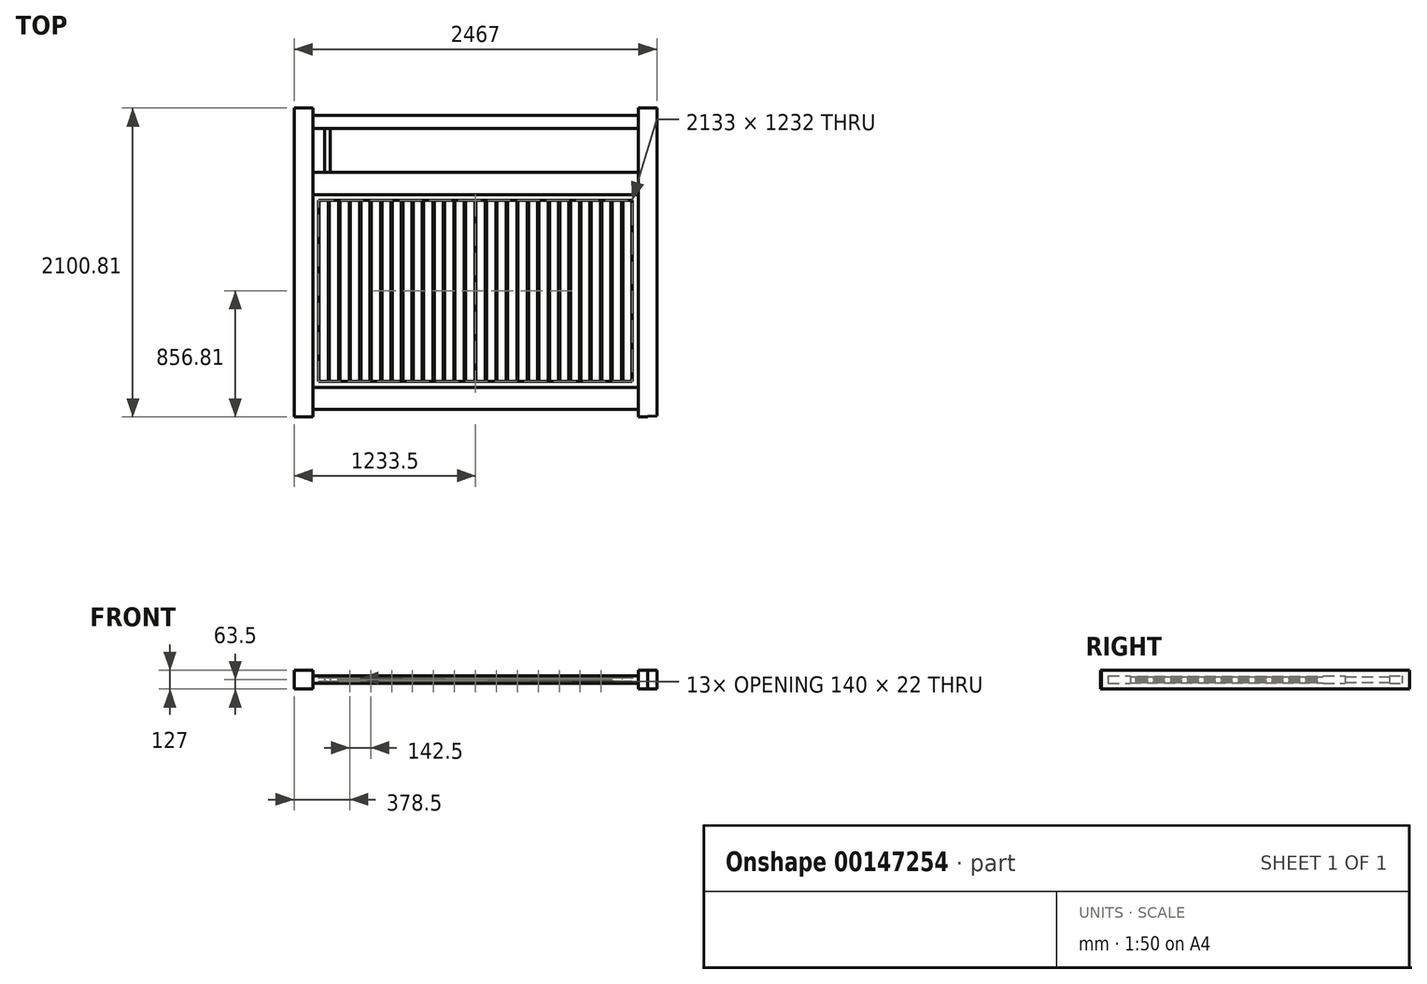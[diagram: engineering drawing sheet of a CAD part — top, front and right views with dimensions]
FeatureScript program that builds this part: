
annotation { "Feature Type Name" : "Feature", "Feature Type Description" : "" }
export const myFeature = defineFeature(function(context is Context, id is Id, definition is map)
    precondition{}
    {
        {
            var Q0;
            Q0=qCreatedBy(makeId("Top.planeOp"),FACE);
            var sketch = newSketch(context, id + "F0", { "sketchPlane" : qUnion([Q0])});
            skLineSegment(sketch, "E0.bottom", {"start": v(1170, -1050) * mm, "end": v(1106.5, -1050) * mm});
            skLineSegment(sketch, "E0.top", {"start": v(1170, 1050) * mm, "end": v(1106.5, 1050) * mm});
            skLineSegment(sketch, "E0.left", {"start": v(1170, -1050) * mm, "end": v(1170, -1047.62) * mm});
            skPoint(sketch, "E0.middle", {"position": v(0, 0) * mm});
            skLineSegment(sketch, "E1", {"start": v(-1170, 1050) * mm, "end": v(-1233.5, 1050) * mm});
            skLineSegment(sketch, "E2", {"start": v(-1233.5, 1050) * mm, "end": v(-1233.5, -1050.8) * mm});
            skLineSegment(sketch, "E3", {"start": v(-1233.5, -1050.8) * mm, "end": v(-1106.5, -1050) * mm});
            skLineSegment(sketch, "E4", {"start": v(-1106.5, -1050) * mm, "end": v(-1106.5, 1050) * mm});
            skLineSegment(sketch, "E5", {"start": v(-1106.5, 1050) * mm, "end": v(-1233.5, 1050) * mm});
            skLineSegment(sketch, "E6", {"start": v(1106.5, -1050) * mm, "end": v(1106.5, 1050) * mm});
            skLineSegment(sketch, "E7", {"start": v(1106.5, 1050) * mm, "end": v(1233.5, 1050) * mm});
            skLineSegment(sketch, "E8", {"start": v(1233.5, 1050) * mm, "end": v(1233.5, -1045.25) * mm});
            skLineSegment(sketch, "E9", {"start": v(1233.5, -1045.25) * mm, "end": v(1106.5, -1050) * mm});
            skLineSegment(sketch, "E10", {"start": v(-1106.5, 1000) * mm, "end": v(1106.5, 1000) * mm});
            skLineSegment(sketch, "E11", {"start": v(1106.5, 1000) * mm, "end": v(1106.5, 912) * mm});
            skLineSegment(sketch, "E12", {"start": v(1106.5, 912) * mm, "end": v(-1106.5, 912) * mm});
            skLineSegment(sketch, "E13", {"start": v(-1106.5, 912) * mm, "end": v(-1106.5, 1000) * mm});
            skLineSegment(sketch, "E14", {"start": v(-1106.5, 612) * mm, "end": v(1106.5, 612) * mm});
            skLineSegment(sketch, "E15", {"start": v(1106.5, 612) * mm, "end": v(1106.5, 462) * mm});
            skLineSegment(sketch, "E16", {"start": v(1106.5, 462) * mm, "end": v(-1106.5, 462) * mm});
            skLineSegment(sketch, "E17", {"start": v(-1106.5, 462) * mm, "end": v(-1106.5, 612) * mm});
            skLineSegment(sketch, "E18", {"start": v(-1106.5, -1000) * mm, "end": v(1106.5, -1000) * mm});
            skLineSegment(sketch, "E19", {"start": v(1106.5, -1000) * mm, "end": v(1106.5, -850) * mm});
            skLineSegment(sketch, "E20", {"start": v(1106.5, -850) * mm, "end": v(-1106.5, -850) * mm});
            skLineSegment(sketch, "E21", {"start": v(-1106.5, -850) * mm, "end": v(-1106.5, -1000) * mm});
            skLineSegment(sketch, "E22", {"start": v(-1106.5, -810) * mm, "end": v(1106.5, -810) * mm});
            skLineSegment(sketch, "E23", {"start": v(-1106.5, 422) * mm, "end": v(1106.5, 422) * mm});
            skLineSegment(sketch, "E24", {"start": v(-1066.5, 422) * mm, "end": v(-1066.5, -810) * mm});
            skLineSegment(sketch, "E25", {"start": v(1066.5, 422) * mm, "end": v(1066.5, -810) * mm});
            skLineSegment(sketch, "E26.trimOffspring", {"start": v(-1106.5, 1050) * mm, "end": v(-1170, 1050) * mm});
            skLineSegment(sketch, "E27.trimOffspring", {"start": v(-1106.5, -1050) * mm, "end": v(-1170, -1050) * mm});
            skLineSegment(sketch, "E28", {"start": v(-1106.5, 1000) * mm, "end": v(-1106.5, 912) * mm});
            skLineSegment(sketch, "E29", {"start": v(1106.5, 912) * mm, "end": v(1106.5, 1000) * mm});
            skLineSegment(sketch, "E30", {"start": v(-1026.03, 912) * mm, "end": v(-1026.03, 612) * mm});
            skLineSegment(sketch, "E31", {"start": v(-1026.03, 612) * mm, "end": v(-988.03, 612) * mm});
            skLineSegment(sketch, "E32", {"start": v(-988.03, 612) * mm, "end": v(-988.03, 912) * mm});
            skLineSegment(sketch, "E33", {"start": v(-988.03, 912) * mm, "end": v(-1026.03, 912) * mm});
            skLineSegment(sketch, "E34.1.0.0", {"start": v(-869.56, 912) * mm, "end": v(-907.56, 912) * mm});
            skLineSegment(sketch, "E34.1.0.1", {"start": v(-907.56, 912) * mm, "end": v(-907.56, 612) * mm});
            skLineSegment(sketch, "E34.1.0.2", {"start": v(-869.56, 612) * mm, "end": v(-869.56, 912) * mm});
            skLineSegment(sketch, "E34.1.0.3", {"start": v(-907.56, 612) * mm, "end": v(-869.56, 612) * mm});
            skLineSegment(sketch, "E34.2.0.0", {"start": v(-751.1, 912) * mm, "end": v(-789.1, 912) * mm});
            skLineSegment(sketch, "E34.2.0.1", {"start": v(-789.1, 912) * mm, "end": v(-789.1, 612) * mm});
            skLineSegment(sketch, "E34.2.0.2", {"start": v(-751.1, 612) * mm, "end": v(-751.1, 912) * mm});
            skLineSegment(sketch, "E34.2.0.3", {"start": v(-789.1, 612) * mm, "end": v(-751.1, 612) * mm});
            skLineSegment(sketch, "E34.3.0.0", {"start": v(-632.62, 912) * mm, "end": v(-670.62, 912) * mm});
            skLineSegment(sketch, "E34.3.0.1", {"start": v(-670.62, 912) * mm, "end": v(-670.62, 612) * mm});
            skLineSegment(sketch, "E34.3.0.2", {"start": v(-632.62, 612) * mm, "end": v(-632.62, 912) * mm});
            skLineSegment(sketch, "E34.3.0.3", {"start": v(-670.62, 612) * mm, "end": v(-632.62, 612) * mm});
            skLineSegment(sketch, "E34.4.0.0", {"start": v(-514.15, 912) * mm, "end": v(-552.15, 912) * mm});
            skLineSegment(sketch, "E34.4.0.1", {"start": v(-552.15, 912) * mm, "end": v(-552.15, 612) * mm});
            skLineSegment(sketch, "E34.4.0.2", {"start": v(-514.15, 612) * mm, "end": v(-514.15, 912) * mm});
            skLineSegment(sketch, "E34.4.0.3", {"start": v(-552.15, 612) * mm, "end": v(-514.15, 612) * mm});
            skLineSegment(sketch, "E34.5.0.0", {"start": v(-395.68, 912) * mm, "end": v(-433.68, 912) * mm});
            skLineSegment(sketch, "E34.5.0.1", {"start": v(-433.68, 912) * mm, "end": v(-433.68, 612) * mm});
            skLineSegment(sketch, "E34.5.0.2", {"start": v(-395.68, 612) * mm, "end": v(-395.68, 912) * mm});
            skLineSegment(sketch, "E34.5.0.3", {"start": v(-433.68, 612) * mm, "end": v(-395.68, 612) * mm});
            skLineSegment(sketch, "E34.6.0.0", {"start": v(-277.21, 912) * mm, "end": v(-315.21, 912) * mm});
            skLineSegment(sketch, "E34.6.0.1", {"start": v(-315.21, 912) * mm, "end": v(-315.21, 612) * mm});
            skLineSegment(sketch, "E34.6.0.2", {"start": v(-277.21, 612) * mm, "end": v(-277.21, 912) * mm});
            skLineSegment(sketch, "E34.6.0.3", {"start": v(-315.21, 612) * mm, "end": v(-277.21, 612) * mm});
            skLineSegment(sketch, "E34.7.0.0", {"start": v(-158.74, 912) * mm, "end": v(-196.74, 912) * mm});
            skLineSegment(sketch, "E34.7.0.1", {"start": v(-196.74, 912) * mm, "end": v(-196.74, 612) * mm});
            skLineSegment(sketch, "E34.7.0.2", {"start": v(-158.74, 612) * mm, "end": v(-158.74, 912) * mm});
            skLineSegment(sketch, "E34.7.0.3", {"start": v(-196.74, 612) * mm, "end": v(-158.74, 612) * mm});
            skLineSegment(sketch, "E34.8.0.0", {"start": v(-40.27, 912) * mm, "end": v(-78.27, 912) * mm});
            skLineSegment(sketch, "E34.8.0.1", {"start": v(-78.27, 912) * mm, "end": v(-78.27, 612) * mm});
            skLineSegment(sketch, "E34.8.0.2", {"start": v(-40.27, 612) * mm, "end": v(-40.27, 912) * mm});
            skLineSegment(sketch, "E34.8.0.3", {"start": v(-78.27, 612) * mm, "end": v(-40.27, 612) * mm});
            skLineSegment(sketch, "E34.9.0.0", {"start": v(78.2, 912) * mm, "end": v(40.2, 912) * mm});
            skLineSegment(sketch, "E34.9.0.1", {"start": v(40.2, 912) * mm, "end": v(40.2, 612) * mm});
            skLineSegment(sketch, "E34.9.0.2", {"start": v(78.2, 612) * mm, "end": v(78.2, 912) * mm});
            skLineSegment(sketch, "E34.9.0.3", {"start": v(40.2, 612) * mm, "end": v(78.2, 612) * mm});
            skLineSegment(sketch, "E34.10.0.0", {"start": v(196.67, 912) * mm, "end": v(158.67, 912) * mm});
            skLineSegment(sketch, "E34.10.0.1", {"start": v(158.67, 912) * mm, "end": v(158.67, 612) * mm});
            skLineSegment(sketch, "E34.10.0.2", {"start": v(196.67, 612) * mm, "end": v(196.67, 912) * mm});
            skLineSegment(sketch, "E34.10.0.3", {"start": v(158.67, 612) * mm, "end": v(196.67, 612) * mm});
            skLineSegment(sketch, "E34.11.0.0", {"start": v(315.14, 912) * mm, "end": v(277.14, 912) * mm});
            skLineSegment(sketch, "E34.11.0.1", {"start": v(277.14, 912) * mm, "end": v(277.14, 612) * mm});
            skLineSegment(sketch, "E34.11.0.2", {"start": v(315.14, 612) * mm, "end": v(315.14, 912) * mm});
            skLineSegment(sketch, "E34.11.0.3", {"start": v(277.14, 612) * mm, "end": v(315.14, 612) * mm});
            skLineSegment(sketch, "E34.12.0.0", {"start": v(433.6, 912) * mm, "end": v(395.6, 912) * mm});
            skLineSegment(sketch, "E34.12.0.1", {"start": v(395.6, 912) * mm, "end": v(395.6, 612) * mm});
            skLineSegment(sketch, "E34.12.0.2", {"start": v(433.6, 612) * mm, "end": v(433.6, 912) * mm});
            skLineSegment(sketch, "E34.12.0.3", {"start": v(395.6, 612) * mm, "end": v(433.6, 612) * mm});
            skLineSegment(sketch, "E34.13.0.0", {"start": v(552.08, 912) * mm, "end": v(514.08, 912) * mm});
            skLineSegment(sketch, "E34.13.0.1", {"start": v(514.08, 912) * mm, "end": v(514.08, 612) * mm});
            skLineSegment(sketch, "E34.13.0.2", {"start": v(552.08, 612) * mm, "end": v(552.08, 912) * mm});
            skLineSegment(sketch, "E34.13.0.3", {"start": v(514.08, 612) * mm, "end": v(552.08, 612) * mm});
            skLineSegment(sketch, "E34.14.0.0", {"start": v(670.55, 912) * mm, "end": v(632.55, 912) * mm});
            skLineSegment(sketch, "E34.14.0.1", {"start": v(632.55, 912) * mm, "end": v(632.55, 612) * mm});
            skLineSegment(sketch, "E34.14.0.2", {"start": v(670.55, 612) * mm, "end": v(670.55, 912) * mm});
            skLineSegment(sketch, "E34.14.0.3", {"start": v(632.55, 612) * mm, "end": v(670.55, 612) * mm});
            skLineSegment(sketch, "E34.15.0.0", {"start": v(789.02, 912) * mm, "end": v(751.02, 912) * mm});
            skLineSegment(sketch, "E34.15.0.1", {"start": v(751.02, 912) * mm, "end": v(751.02, 612) * mm});
            skLineSegment(sketch, "E34.15.0.2", {"start": v(789.02, 612) * mm, "end": v(789.02, 912) * mm});
            skLineSegment(sketch, "E34.15.0.3", {"start": v(751.02, 612) * mm, "end": v(789.02, 612) * mm});
            skLineSegment(sketch, "E34.16.0.0", {"start": v(907.49, 912) * mm, "end": v(869.49, 912) * mm});
            skLineSegment(sketch, "E34.16.0.1", {"start": v(869.49, 912) * mm, "end": v(869.49, 612) * mm});
            skLineSegment(sketch, "E34.16.0.2", {"start": v(907.49, 612) * mm, "end": v(907.49, 912) * mm});
            skLineSegment(sketch, "E34.16.0.3", {"start": v(869.49, 612) * mm, "end": v(907.49, 612) * mm});
            skLineSegment(sketch, "E34.17.0.0", {"start": v(1025.96, 912) * mm, "end": v(987.96, 912) * mm});
            skLineSegment(sketch, "E34.17.0.1", {"start": v(987.96, 912) * mm, "end": v(987.96, 612) * mm});
            skLineSegment(sketch, "E34.17.0.2", {"start": v(1025.96, 612) * mm, "end": v(1025.96, 912) * mm});
            skLineSegment(sketch, "E34.17.0.3", {"start": v(987.96, 612) * mm, "end": v(1025.96, 612) * mm});
            skLineSegment(sketch, "E34.direction1", {"start": v(-1026.03, 912) * mm, "end": v(-907.56, 912) * mm, "construction": true});
            skSolve(sketch);
        }
        {
            var Q0;
            {var subQ0=sQuery(id+"F0.wireOp",EDGE,"E0.left");Q0=makeQuery(id+"F0.imprint","IMPRINT",FACE,{"disambiguationData":[TD([[makeQuery(id+"F0.imprint","IMPRINT",EDGE,{"derivedFrom":subQ0}),1.0]])]});}
            var Q1;
            Q1=makeQuery(id+"F0.imprint","IMPRINT",FACE,{"disambiguationData":[TD([[makeQuery(id+"F0.imprint","IMPRINT",EDGE,{"derivedFrom":sQuery(id+"F0.wireOp",EDGE,"E2")}),1.0]])]});
            var Q2;
            {var subQ6=sQuery(id+"F0.wireOp",EDGE,"E8");Q2=makeQuery(id+"F0.imprint","IMPRINT",FACE,{"disambiguationData":[TD([[makeQuery(id+"F0.imprint","IMPRINT",EDGE,{"derivedFrom":subQ6}),-1.0]])]});}
            extrude(context, id + "F1", {"entities" : qUnion([Q0, Q1, Q2]), "depth" : 63.5 * mm, "hasSecondDirection" : true, "secondDirectionOppositeDirection" : true, "secondDirectionDepth" : 63.5 * mm});
        }
        {
            var Q0;
            Q0=makeQuery(id+"F0.imprint","IMPRINT",FACE,{"disambiguationData":[TD([[makeQuery(id+"F0.imprint","IMPRINT",EDGE,{"derivedFrom":sQuery(id+"F0.wireOp",EDGE,"E10")}),-1.0]])]});
            var Q1;
            Q1=makeQuery(id+"F0.imprint","IMPRINT",FACE,{"disambiguationData":[TD([[makeQuery(id+"F0.imprint","IMPRINT",EDGE,{"derivedFrom":sQuery(id+"F0.wireOp",EDGE,"E14")}),-1.0]])]});
            var Q2;
            Q2=makeQuery(id+"F0.imprint","IMPRINT",FACE,{"disambiguationData":[TD([[makeQuery(id+"F0.imprint","IMPRINT",EDGE,{"derivedFrom":sQuery(id+"F0.wireOp",EDGE,"E18")}),1.0]])]});
            extrude(context, id + "F2", {"entities" : qUnion([Q0, Q1, Q2]), "depth" : 25 * mm, "hasSecondDirection" : true, "secondDirectionOppositeDirection" : true, "secondDirectionDepth" : 25 * mm});
        }
        {
            var Q0;
            {var subQ0=sQuery(id+"F0.wireOp",EDGE,"E16");Q0=makeQuery(id+"F0.imprint","IMPRINT",FACE,{"disambiguationData":[TD([[makeQuery(id+"F0.imprint","IMPRINT",EDGE,{"derivedFrom":subQ0}),1.0]])]});}
            var Q1;
            {var subQ5=sQuery(id+"F0.wireOp",EDGE,"E25");Q1=makeQuery(id+"F0.imprint","IMPRINT",FACE,{"disambiguationData":[TD([[makeQuery(id+"F0.imprint","IMPRINT",EDGE,{"derivedFrom":subQ5}),1.0]])]});}
            var Q2;
            {var subQ4=sQuery(id+"F0.wireOp",EDGE,"E20");Q2=makeQuery(id+"F0.imprint","IMPRINT",FACE,{"disambiguationData":[TD([[makeQuery(id+"F0.imprint","IMPRINT",EDGE,{"derivedFrom":subQ4}),-1.0]])]});}
            var Q3;
            {var subQ5=sQuery(id+"F0.wireOp",EDGE,"E24");Q3=makeQuery(id+"F0.imprint","IMPRINT",FACE,{"disambiguationData":[TD([[makeQuery(id+"F0.imprint","IMPRINT",EDGE,{"derivedFrom":subQ5}),-1.0]])]});}
            extrude(context, id + "F3", {"entities" : qUnion([Q0, Q1, Q2, Q3]), "depth" : 20 * mm, "hasSecondDirection" : true, "secondDirectionOppositeDirection" : true, "secondDirectionDepth" : 20 * mm});
        }
        {
            var Q0;
            Q0=makeQuery(id+"F0.imprint","IMPRINT",FACE,{"disambiguationData":[TD([[makeQuery(id+"F0.imprint","IMPRINT",EDGE,{"derivedFrom":sQuery(id+"F0.wireOp",EDGE,"E30")}),1.0]])]});
            var Q1;
            Q1=makeQuery(id+"F0.imprint","IMPRINT",FACE,{"disambiguationData":[TD([[makeQuery(id+"F0.imprint","IMPRINT",EDGE,{"derivedFrom":sQuery(id+"F0.wireOp",EDGE,"E34.1.0.0")}),1.0]])]});
            var Q2;
            Q2=makeQuery(id+"F0.imprint","IMPRINT",FACE,{"disambiguationData":[TD([[makeQuery(id+"F0.imprint","IMPRINT",EDGE,{"derivedFrom":sQuery(id+"F0.wireOp",EDGE,"E34.2.0.0")}),1.0]])]});
            var Q3;
            Q3=makeQuery(id+"F0.imprint","IMPRINT",FACE,{"disambiguationData":[TD([[makeQuery(id+"F0.imprint","IMPRINT",EDGE,{"derivedFrom":sQuery(id+"F0.wireOp",EDGE,"E34.3.0.0")}),1.0]])]});
            var Q4;
            Q4=makeQuery(id+"F0.imprint","IMPRINT",FACE,{"disambiguationData":[TD([[makeQuery(id+"F0.imprint","IMPRINT",EDGE,{"derivedFrom":sQuery(id+"F0.wireOp",EDGE,"E34.4.0.0")}),1.0]])]});
            var Q5;
            Q5=makeQuery(id+"F0.imprint","IMPRINT",FACE,{"disambiguationData":[TD([[makeQuery(id+"F0.imprint","IMPRINT",EDGE,{"derivedFrom":sQuery(id+"F0.wireOp",EDGE,"E34.5.0.0")}),1.0]])]});
            var Q6;
            Q6=makeQuery(id+"F0.imprint","IMPRINT",FACE,{"disambiguationData":[TD([[makeQuery(id+"F0.imprint","IMPRINT",EDGE,{"derivedFrom":sQuery(id+"F0.wireOp",EDGE,"E34.6.0.0")}),1.0]])]});
            var Q7;
            Q7=makeQuery(id+"F0.imprint","IMPRINT",FACE,{"disambiguationData":[TD([[makeQuery(id+"F0.imprint","IMPRINT",EDGE,{"derivedFrom":sQuery(id+"F0.wireOp",EDGE,"E34.7.0.0")}),1.0]])]});
            var Q8;
            Q8=makeQuery(id+"F0.imprint","IMPRINT",FACE,{"disambiguationData":[TD([[makeQuery(id+"F0.imprint","IMPRINT",EDGE,{"derivedFrom":sQuery(id+"F0.wireOp",EDGE,"E34.8.0.0")}),1.0]])]});
            var Q9;
            Q9=makeQuery(id+"F0.imprint","IMPRINT",FACE,{"disambiguationData":[TD([[makeQuery(id+"F0.imprint","IMPRINT",EDGE,{"derivedFrom":sQuery(id+"F0.wireOp",EDGE,"E34.9.0.0")}),1.0]])]});
            var Q10;
            Q10=makeQuery(id+"F0.imprint","IMPRINT",FACE,{"disambiguationData":[TD([[makeQuery(id+"F0.imprint","IMPRINT",EDGE,{"derivedFrom":sQuery(id+"F0.wireOp",EDGE,"E34.10.0.0")}),1.0]])]});
            var Q11;
            Q11=makeQuery(id+"F0.imprint","IMPRINT",FACE,{"disambiguationData":[TD([[makeQuery(id+"F0.imprint","IMPRINT",EDGE,{"derivedFrom":sQuery(id+"F0.wireOp",EDGE,"E34.11.0.0")}),1.0]])]});
            var Q12;
            Q12=makeQuery(id+"F0.imprint","IMPRINT",FACE,{"disambiguationData":[TD([[makeQuery(id+"F0.imprint","IMPRINT",EDGE,{"derivedFrom":sQuery(id+"F0.wireOp",EDGE,"E34.12.0.0")}),1.0]])]});
            var Q13;
            Q13=makeQuery(id+"F0.imprint","IMPRINT",FACE,{"disambiguationData":[TD([[makeQuery(id+"F0.imprint","IMPRINT",EDGE,{"derivedFrom":sQuery(id+"F0.wireOp",EDGE,"E34.13.0.0")}),1.0]])]});
            var Q14;
            Q14=makeQuery(id+"F0.imprint","IMPRINT",FACE,{"disambiguationData":[TD([[makeQuery(id+"F0.imprint","IMPRINT",EDGE,{"derivedFrom":sQuery(id+"F0.wireOp",EDGE,"E34.14.0.0")}),1.0]])]});
            var Q15;
            Q15=makeQuery(id+"F0.imprint","IMPRINT",FACE,{"disambiguationData":[TD([[makeQuery(id+"F0.imprint","IMPRINT",EDGE,{"derivedFrom":sQuery(id+"F0.wireOp",EDGE,"E34.15.0.0")}),1.0]])]});
            var Q16;
            Q16=makeQuery(id+"F0.imprint","IMPRINT",FACE,{"disambiguationData":[TD([[makeQuery(id+"F0.imprint","IMPRINT",EDGE,{"derivedFrom":sQuery(id+"F0.wireOp",EDGE,"E34.16.0.0")}),1.0]])]});
            var Q17;
            Q17=makeQuery(id+"F0.imprint","IMPRINT",FACE,{"disambiguationData":[TD([[makeQuery(id+"F0.imprint","IMPRINT",EDGE,{"derivedFrom":sQuery(id+"F0.wireOp",EDGE,"E34.17.0.0")}),1.0]])]});
            extrude(context, id + "F4", {"entities" : qUnion([Q0, Q1, Q2, Q3, Q4, Q5, Q6, Q7, Q8, Q9, Q10, Q11, Q12, Q13, Q14, Q15, Q16, Q17]), "depth" : 19 * mm, "hasSecondDirection" : true, "secondDirectionOppositeDirection" : true, "secondDirectionDepth" : 19 * mm});
        }
        {
            var Q0;
            Q0=qCreatedBy(makeId("Front.planeOp"),FACE);
            var sketch = newSketch(context, id + "F5", { "sketchPlane" : qUnion([Q0])});
            skLineSegment(sketch, "E35.bottom", {"start": v(-931.2, -11) * mm, "end": v(-992.5, -11) * mm});
            skLineSegment(sketch, "E35.top", {"start": v(-930.95, 11) * mm, "end": v(-993.4, 11) * mm});
            skLineSegment(sketch, "E35.left", {"start": v(-927.5, -7.64) * mm, "end": v(-927.5, 7.38) * mm});
            skLineSegment(sketch, "E35.right", {"start": v(-1067.5, -8.32) * mm, "end": v(-1067.5, 7.65) * mm});
            skLineSegment(sketch, "E36", {"start": v(-1063.8, 11) * mm, "end": v(-1067.5, 7.65) * mm});
            skLineSegment(sketch, "E37", {"start": v(-1067.5, -8.32) * mm, "end": v(-1063.28, -11) * mm});
            skLineSegment(sketch, "E38", {"start": v(-930.95, 11) * mm, "end": v(-927.5, 7.38) * mm});
            skLineSegment(sketch, "E39", {"start": v(-927.5, -7.64) * mm, "end": v(-931.2, -11) * mm});
            skPoint(sketch, "E40.orphan", {"position": v(-927.5, -11) * mm});
            skPoint(sketch, "E41.orphan", {"position": v(-927.5, 11) * mm});
            skPoint(sketch, "E42.orphan", {"position": v(-1067.5, -11) * mm});
            skPoint(sketch, "E43.orphan", {"position": v(-1067.5, 11) * mm});
            skLineSegment(sketch, "E44", {"start": v(-1000.5, -11) * mm, "end": v(-996.5, -8) * mm});
            skLineSegment(sketch, "E45", {"start": v(-996.5, -8) * mm, "end": v(-992.5, -11) * mm});
            skLineSegment(sketch, "E46", {"start": v(-1001.4, 11) * mm, "end": v(-997.4, 8) * mm});
            skLineSegment(sketch, "E47", {"start": v(-997.4, 8) * mm, "end": v(-993.4, 11) * mm});
            skLineSegment(sketch, "E48.trimOffspring", {"start": v(-1001.4, 11) * mm, "end": v(-1063.8, 11) * mm});
            skPoint(sketch, "E49.orphan", {"position": v(0, 18.02) * mm});
            skLineSegment(sketch, "E50.trimOffspring", {"start": v(-1000.5, -11) * mm, "end": v(-1063.28, -11) * mm});
            skLineSegment(sketch, "E51.1.0.0", {"start": v(-858, -11) * mm, "end": v(-920.78, -11) * mm});
            skLineSegment(sketch, "E51.1.0.1", {"start": v(-925, -8.32) * mm, "end": v(-925, 7.65) * mm});
            skPoint(sketch, "E51.1.0.2", {"position": v(-785, 11) * mm});
            skPoint(sketch, "E51.1.0.3", {"position": v(-925, -11) * mm});
            skLineSegment(sketch, "E51.1.0.4", {"start": v(-785, -7.64) * mm, "end": v(-785, 7.38) * mm});
            skPoint(sketch, "E51.1.0.5", {"position": v(-785, -11) * mm});
            skLineSegment(sketch, "E51.1.0.6", {"start": v(-788.45, 11) * mm, "end": v(-850.9, 11) * mm});
            skLineSegment(sketch, "E51.1.0.7", {"start": v(-788.7, -11) * mm, "end": v(-850, -11) * mm});
            skLineSegment(sketch, "E51.1.0.8", {"start": v(-858.9, 11) * mm, "end": v(-921.3, 11) * mm});
            skPoint(sketch, "E51.1.0.9", {"position": v(-925, 11) * mm});
            skLineSegment(sketch, "E51.1.0.10", {"start": v(-921.3, 11) * mm, "end": v(-925, 7.65) * mm});
            skLineSegment(sketch, "E51.1.0.11", {"start": v(-854, -8) * mm, "end": v(-850, -11) * mm});
            skLineSegment(sketch, "E51.1.0.12", {"start": v(-925, -8.32) * mm, "end": v(-920.78, -11) * mm});
            skLineSegment(sketch, "E51.1.0.13", {"start": v(-788.45, 11) * mm, "end": v(-785, 7.38) * mm});
            skLineSegment(sketch, "E51.1.0.14", {"start": v(-858, -11) * mm, "end": v(-854, -8) * mm});
            skLineSegment(sketch, "E51.1.0.15", {"start": v(-785, -7.64) * mm, "end": v(-788.7, -11) * mm});
            skLineSegment(sketch, "E51.1.0.16", {"start": v(-854.9, 8) * mm, "end": v(-850.9, 11) * mm});
            skLineSegment(sketch, "E51.1.0.17", {"start": v(-858.9, 11) * mm, "end": v(-854.9, 8) * mm});
            skLineSegment(sketch, "E51.2.0.0", {"start": v(-715.5, -11) * mm, "end": v(-778.28, -11) * mm});
            skLineSegment(sketch, "E51.2.0.1", {"start": v(-782.5, -8.32) * mm, "end": v(-782.5, 7.65) * mm});
            skPoint(sketch, "E51.2.0.2", {"position": v(-642.5, 11) * mm});
            skPoint(sketch, "E51.2.0.3", {"position": v(-782.5, -11) * mm});
            skLineSegment(sketch, "E51.2.0.4", {"start": v(-642.5, -7.64) * mm, "end": v(-642.5, 7.38) * mm});
            skPoint(sketch, "E51.2.0.5", {"position": v(-642.5, -11) * mm});
            skLineSegment(sketch, "E51.2.0.6", {"start": v(-645.95, 11) * mm, "end": v(-708.4, 11) * mm});
            skLineSegment(sketch, "E51.2.0.7", {"start": v(-646.2, -11) * mm, "end": v(-707.5, -11) * mm});
            skLineSegment(sketch, "E51.2.0.8", {"start": v(-716.4, 11) * mm, "end": v(-778.8, 11) * mm});
            skPoint(sketch, "E51.2.0.9", {"position": v(-782.5, 11) * mm});
            skLineSegment(sketch, "E51.2.0.10", {"start": v(-778.8, 11) * mm, "end": v(-782.5, 7.65) * mm});
            skLineSegment(sketch, "E51.2.0.11", {"start": v(-711.5, -8) * mm, "end": v(-707.5, -11) * mm});
            skLineSegment(sketch, "E51.2.0.12", {"start": v(-782.5, -8.32) * mm, "end": v(-778.28, -11) * mm});
            skLineSegment(sketch, "E51.2.0.13", {"start": v(-645.95, 11) * mm, "end": v(-642.5, 7.38) * mm});
            skLineSegment(sketch, "E51.2.0.14", {"start": v(-715.5, -11) * mm, "end": v(-711.5, -8) * mm});
            skLineSegment(sketch, "E51.2.0.15", {"start": v(-642.5, -7.64) * mm, "end": v(-646.2, -11) * mm});
            skLineSegment(sketch, "E51.2.0.16", {"start": v(-712.4, 8) * mm, "end": v(-708.4, 11) * mm});
            skLineSegment(sketch, "E51.2.0.17", {"start": v(-716.4, 11) * mm, "end": v(-712.4, 8) * mm});
            skLineSegment(sketch, "E51.3.0.0", {"start": v(-573, -11) * mm, "end": v(-635.78, -11) * mm});
            skLineSegment(sketch, "E51.3.0.1", {"start": v(-640, -8.32) * mm, "end": v(-640, 7.65) * mm});
            skPoint(sketch, "E51.3.0.2", {"position": v(-500, 11) * mm});
            skPoint(sketch, "E51.3.0.3", {"position": v(-640, -11) * mm});
            skLineSegment(sketch, "E51.3.0.4", {"start": v(-500, -7.64) * mm, "end": v(-500, 7.38) * mm});
            skPoint(sketch, "E51.3.0.5", {"position": v(-500, -11) * mm});
            skLineSegment(sketch, "E51.3.0.6", {"start": v(-503.45, 11) * mm, "end": v(-565.9, 11) * mm});
            skLineSegment(sketch, "E51.3.0.7", {"start": v(-503.7, -11) * mm, "end": v(-565, -11) * mm});
            skLineSegment(sketch, "E51.3.0.8", {"start": v(-573.9, 11) * mm, "end": v(-636.3, 11) * mm});
            skPoint(sketch, "E51.3.0.9", {"position": v(-640, 11) * mm});
            skLineSegment(sketch, "E51.3.0.10", {"start": v(-636.3, 11) * mm, "end": v(-640, 7.65) * mm});
            skLineSegment(sketch, "E51.3.0.11", {"start": v(-569, -8) * mm, "end": v(-565, -11) * mm});
            skLineSegment(sketch, "E51.3.0.12", {"start": v(-640, -8.32) * mm, "end": v(-635.78, -11) * mm});
            skLineSegment(sketch, "E51.3.0.13", {"start": v(-503.45, 11) * mm, "end": v(-500, 7.38) * mm});
            skLineSegment(sketch, "E51.3.0.14", {"start": v(-573, -11) * mm, "end": v(-569, -8) * mm});
            skLineSegment(sketch, "E51.3.0.15", {"start": v(-500, -7.64) * mm, "end": v(-503.7, -11) * mm});
            skLineSegment(sketch, "E51.3.0.16", {"start": v(-569.9, 8) * mm, "end": v(-565.9, 11) * mm});
            skLineSegment(sketch, "E51.3.0.17", {"start": v(-573.9, 11) * mm, "end": v(-569.9, 8) * mm});
            skLineSegment(sketch, "E51.4.0.0", {"start": v(-430.5, -11) * mm, "end": v(-493.28, -11) * mm});
            skLineSegment(sketch, "E51.4.0.1", {"start": v(-497.5, -8.32) * mm, "end": v(-497.5, 7.65) * mm});
            skPoint(sketch, "E51.4.0.2", {"position": v(-357.5, 11) * mm});
            skPoint(sketch, "E51.4.0.3", {"position": v(-497.5, -11) * mm});
            skLineSegment(sketch, "E51.4.0.4", {"start": v(-357.5, -7.64) * mm, "end": v(-357.5, 7.38) * mm});
            skPoint(sketch, "E51.4.0.5", {"position": v(-357.5, -11) * mm});
            skLineSegment(sketch, "E51.4.0.6", {"start": v(-360.95, 11) * mm, "end": v(-423.4, 11) * mm});
            skLineSegment(sketch, "E51.4.0.7", {"start": v(-361.2, -11) * mm, "end": v(-422.5, -11) * mm});
            skLineSegment(sketch, "E51.4.0.8", {"start": v(-431.4, 11) * mm, "end": v(-493.8, 11) * mm});
            skPoint(sketch, "E51.4.0.9", {"position": v(-497.5, 11) * mm});
            skLineSegment(sketch, "E51.4.0.10", {"start": v(-493.8, 11) * mm, "end": v(-497.5, 7.65) * mm});
            skLineSegment(sketch, "E51.4.0.11", {"start": v(-426.5, -8) * mm, "end": v(-422.5, -11) * mm});
            skLineSegment(sketch, "E51.4.0.12", {"start": v(-497.5, -8.32) * mm, "end": v(-493.28, -11) * mm});
            skLineSegment(sketch, "E51.4.0.13", {"start": v(-360.95, 11) * mm, "end": v(-357.5, 7.38) * mm});
            skLineSegment(sketch, "E51.4.0.14", {"start": v(-430.5, -11) * mm, "end": v(-426.5, -8) * mm});
            skLineSegment(sketch, "E51.4.0.15", {"start": v(-357.5, -7.64) * mm, "end": v(-361.2, -11) * mm});
            skLineSegment(sketch, "E51.4.0.16", {"start": v(-427.4, 8) * mm, "end": v(-423.4, 11) * mm});
            skLineSegment(sketch, "E51.4.0.17", {"start": v(-431.4, 11) * mm, "end": v(-427.4, 8) * mm});
            skLineSegment(sketch, "E51.5.0.0", {"start": v(-288, -11) * mm, "end": v(-350.78, -11) * mm});
            skLineSegment(sketch, "E51.5.0.1", {"start": v(-355, -8.32) * mm, "end": v(-355, 7.65) * mm});
            skPoint(sketch, "E51.5.0.2", {"position": v(-215, 11) * mm});
            skPoint(sketch, "E51.5.0.3", {"position": v(-355, -11) * mm});
            skLineSegment(sketch, "E51.5.0.4", {"start": v(-215, -7.64) * mm, "end": v(-215, 7.38) * mm});
            skPoint(sketch, "E51.5.0.5", {"position": v(-215, -11) * mm});
            skLineSegment(sketch, "E51.5.0.6", {"start": v(-218.45, 11) * mm, "end": v(-280.9, 11) * mm});
            skLineSegment(sketch, "E51.5.0.7", {"start": v(-218.7, -11) * mm, "end": v(-280, -11) * mm});
            skLineSegment(sketch, "E51.5.0.8", {"start": v(-288.9, 11) * mm, "end": v(-351.3, 11) * mm});
            skPoint(sketch, "E51.5.0.9", {"position": v(-355, 11) * mm});
            skLineSegment(sketch, "E51.5.0.10", {"start": v(-351.3, 11) * mm, "end": v(-355, 7.65) * mm});
            skLineSegment(sketch, "E51.5.0.11", {"start": v(-284, -8) * mm, "end": v(-280, -11) * mm});
            skLineSegment(sketch, "E51.5.0.12", {"start": v(-355, -8.32) * mm, "end": v(-350.78, -11) * mm});
            skLineSegment(sketch, "E51.5.0.13", {"start": v(-218.45, 11) * mm, "end": v(-215, 7.38) * mm});
            skLineSegment(sketch, "E51.5.0.14", {"start": v(-288, -11) * mm, "end": v(-284, -8) * mm});
            skLineSegment(sketch, "E51.5.0.15", {"start": v(-215, -7.64) * mm, "end": v(-218.7, -11) * mm});
            skLineSegment(sketch, "E51.5.0.16", {"start": v(-284.9, 8) * mm, "end": v(-280.9, 11) * mm});
            skLineSegment(sketch, "E51.5.0.17", {"start": v(-288.9, 11) * mm, "end": v(-284.9, 8) * mm});
            skLineSegment(sketch, "E51.6.0.0", {"start": v(-145.5, -11) * mm, "end": v(-208.28, -11) * mm});
            skLineSegment(sketch, "E51.6.0.1", {"start": v(-212.5, -8.32) * mm, "end": v(-212.5, 7.65) * mm});
            skPoint(sketch, "E51.6.0.2", {"position": v(-72.5, 11) * mm});
            skPoint(sketch, "E51.6.0.3", {"position": v(-212.5, -11) * mm});
            skLineSegment(sketch, "E51.6.0.4", {"start": v(-72.5, -7.64) * mm, "end": v(-72.5, 7.38) * mm});
            skPoint(sketch, "E51.6.0.5", {"position": v(-72.5, -11) * mm});
            skLineSegment(sketch, "E51.6.0.6", {"start": v(-75.95, 11) * mm, "end": v(-138.4, 11) * mm});
            skLineSegment(sketch, "E51.6.0.7", {"start": v(-76.2, -11) * mm, "end": v(-137.5, -11) * mm});
            skLineSegment(sketch, "E51.6.0.8", {"start": v(-146.4, 11) * mm, "end": v(-208.8, 11) * mm});
            skPoint(sketch, "E51.6.0.9", {"position": v(-212.5, 11) * mm});
            skLineSegment(sketch, "E51.6.0.10", {"start": v(-208.8, 11) * mm, "end": v(-212.5, 7.65) * mm});
            skLineSegment(sketch, "E51.6.0.11", {"start": v(-141.5, -8) * mm, "end": v(-137.5, -11) * mm});
            skLineSegment(sketch, "E51.6.0.12", {"start": v(-212.5, -8.32) * mm, "end": v(-208.28, -11) * mm});
            skLineSegment(sketch, "E51.6.0.13", {"start": v(-75.95, 11) * mm, "end": v(-72.5, 7.38) * mm});
            skLineSegment(sketch, "E51.6.0.14", {"start": v(-145.5, -11) * mm, "end": v(-141.5, -8) * mm});
            skLineSegment(sketch, "E51.6.0.15", {"start": v(-72.5, -7.64) * mm, "end": v(-76.2, -11) * mm});
            skLineSegment(sketch, "E51.6.0.16", {"start": v(-142.4, 8) * mm, "end": v(-138.4, 11) * mm});
            skLineSegment(sketch, "E51.6.0.17", {"start": v(-146.4, 11) * mm, "end": v(-142.4, 8) * mm});
            skLineSegment(sketch, "E51.7.0.0", {"start": v(-3, -11) * mm, "end": v(-65.78, -11) * mm});
            skLineSegment(sketch, "E51.7.0.1", {"start": v(-70, -8.32) * mm, "end": v(-70, 7.65) * mm});
            skPoint(sketch, "E51.7.0.2", {"position": v(70, 11) * mm});
            skPoint(sketch, "E51.7.0.3", {"position": v(-70, -11) * mm});
            skLineSegment(sketch, "E51.7.0.4", {"start": v(70, -7.64) * mm, "end": v(70, 7.38) * mm});
            skPoint(sketch, "E51.7.0.5", {"position": v(70, -11) * mm});
            skLineSegment(sketch, "E51.7.0.6", {"start": v(66.55, 11) * mm, "end": v(4.1, 11) * mm});
            skLineSegment(sketch, "E51.7.0.7", {"start": v(66.3, -11) * mm, "end": v(5, -11) * mm});
            skLineSegment(sketch, "E51.7.0.8", {"start": v(-3.9, 11) * mm, "end": v(-66.3, 11) * mm});
            skPoint(sketch, "E51.7.0.9", {"position": v(-70, 11) * mm});
            skLineSegment(sketch, "E51.7.0.10", {"start": v(-66.3, 11) * mm, "end": v(-70, 7.65) * mm});
            skLineSegment(sketch, "E51.7.0.11", {"start": v(1, -8) * mm, "end": v(5, -11) * mm});
            skLineSegment(sketch, "E51.7.0.12", {"start": v(-70, -8.32) * mm, "end": v(-65.78, -11) * mm});
            skLineSegment(sketch, "E51.7.0.13", {"start": v(66.55, 11) * mm, "end": v(70, 7.38) * mm});
            skLineSegment(sketch, "E51.7.0.14", {"start": v(-3, -11) * mm, "end": v(1, -8) * mm});
            skLineSegment(sketch, "E51.7.0.15", {"start": v(70, -7.64) * mm, "end": v(66.3, -11) * mm});
            skLineSegment(sketch, "E51.7.0.16", {"start": v(0.1, 8) * mm, "end": v(4.1, 11) * mm});
            skLineSegment(sketch, "E51.7.0.17", {"start": v(-3.9, 11) * mm, "end": v(0.1, 8) * mm});
            skLineSegment(sketch, "E51.8.0.0", {"start": v(139.5, -11) * mm, "end": v(76.72, -11) * mm});
            skLineSegment(sketch, "E51.8.0.1", {"start": v(72.5, -8.32) * mm, "end": v(72.5, 7.65) * mm});
            skPoint(sketch, "E51.8.0.2", {"position": v(212.5, 11) * mm});
            skPoint(sketch, "E51.8.0.3", {"position": v(72.5, -11) * mm});
            skLineSegment(sketch, "E51.8.0.4", {"start": v(212.5, -7.64) * mm, "end": v(212.5, 7.38) * mm});
            skPoint(sketch, "E51.8.0.5", {"position": v(212.5, -11) * mm});
            skLineSegment(sketch, "E51.8.0.6", {"start": v(209.05, 11) * mm, "end": v(146.6, 11) * mm});
            skLineSegment(sketch, "E51.8.0.7", {"start": v(208.8, -11) * mm, "end": v(147.5, -11) * mm});
            skLineSegment(sketch, "E51.8.0.8", {"start": v(138.6, 11) * mm, "end": v(76.2, 11) * mm});
            skPoint(sketch, "E51.8.0.9", {"position": v(72.5, 11) * mm});
            skLineSegment(sketch, "E51.8.0.10", {"start": v(76.2, 11) * mm, "end": v(72.5, 7.65) * mm});
            skLineSegment(sketch, "E51.8.0.11", {"start": v(143.5, -8) * mm, "end": v(147.5, -11) * mm});
            skLineSegment(sketch, "E51.8.0.12", {"start": v(72.5, -8.32) * mm, "end": v(76.72, -11) * mm});
            skLineSegment(sketch, "E51.8.0.13", {"start": v(209.05, 11) * mm, "end": v(212.5, 7.38) * mm});
            skLineSegment(sketch, "E51.8.0.14", {"start": v(139.5, -11) * mm, "end": v(143.5, -8) * mm});
            skLineSegment(sketch, "E51.8.0.15", {"start": v(212.5, -7.64) * mm, "end": v(208.8, -11) * mm});
            skLineSegment(sketch, "E51.8.0.16", {"start": v(142.6, 8) * mm, "end": v(146.6, 11) * mm});
            skLineSegment(sketch, "E51.8.0.17", {"start": v(138.6, 11) * mm, "end": v(142.6, 8) * mm});
            skLineSegment(sketch, "E51.9.0.0", {"start": v(282, -11) * mm, "end": v(219.22, -11) * mm});
            skLineSegment(sketch, "E51.9.0.1", {"start": v(215, -8.32) * mm, "end": v(215, 7.65) * mm});
            skPoint(sketch, "E51.9.0.2", {"position": v(355, 11) * mm});
            skPoint(sketch, "E51.9.0.3", {"position": v(215, -11) * mm});
            skLineSegment(sketch, "E51.9.0.4", {"start": v(355, -7.64) * mm, "end": v(355, 7.38) * mm});
            skPoint(sketch, "E51.9.0.5", {"position": v(355, -11) * mm});
            skLineSegment(sketch, "E51.9.0.6", {"start": v(351.55, 11) * mm, "end": v(289.1, 11) * mm});
            skLineSegment(sketch, "E51.9.0.7", {"start": v(351.3, -11) * mm, "end": v(290, -11) * mm});
            skLineSegment(sketch, "E51.9.0.8", {"start": v(281.1, 11) * mm, "end": v(218.7, 11) * mm});
            skPoint(sketch, "E51.9.0.9", {"position": v(215, 11) * mm});
            skLineSegment(sketch, "E51.9.0.10", {"start": v(218.7, 11) * mm, "end": v(215, 7.65) * mm});
            skLineSegment(sketch, "E51.9.0.11", {"start": v(286, -8) * mm, "end": v(290, -11) * mm});
            skLineSegment(sketch, "E51.9.0.12", {"start": v(215, -8.32) * mm, "end": v(219.22, -11) * mm});
            skLineSegment(sketch, "E51.9.0.13", {"start": v(351.55, 11) * mm, "end": v(355, 7.38) * mm});
            skLineSegment(sketch, "E51.9.0.14", {"start": v(282, -11) * mm, "end": v(286, -8) * mm});
            skLineSegment(sketch, "E51.9.0.15", {"start": v(355, -7.64) * mm, "end": v(351.3, -11) * mm});
            skLineSegment(sketch, "E51.9.0.16", {"start": v(285.1, 8) * mm, "end": v(289.1, 11) * mm});
            skLineSegment(sketch, "E51.9.0.17", {"start": v(281.1, 11) * mm, "end": v(285.1, 8) * mm});
            skLineSegment(sketch, "E51.10.0.0", {"start": v(424.5, -11) * mm, "end": v(361.72, -11) * mm});
            skLineSegment(sketch, "E51.10.0.1", {"start": v(357.5, -8.32) * mm, "end": v(357.5, 7.65) * mm});
            skPoint(sketch, "E51.10.0.2", {"position": v(497.5, 11) * mm});
            skPoint(sketch, "E51.10.0.3", {"position": v(357.5, -11) * mm});
            skLineSegment(sketch, "E51.10.0.4", {"start": v(497.5, -7.64) * mm, "end": v(497.5, 7.38) * mm});
            skPoint(sketch, "E51.10.0.5", {"position": v(497.5, -11) * mm});
            skLineSegment(sketch, "E51.10.0.6", {"start": v(494.05, 11) * mm, "end": v(431.6, 11) * mm});
            skLineSegment(sketch, "E51.10.0.7", {"start": v(493.8, -11) * mm, "end": v(432.5, -11) * mm});
            skLineSegment(sketch, "E51.10.0.8", {"start": v(423.6, 11) * mm, "end": v(361.2, 11) * mm});
            skPoint(sketch, "E51.10.0.9", {"position": v(357.5, 11) * mm});
            skLineSegment(sketch, "E51.10.0.10", {"start": v(361.2, 11) * mm, "end": v(357.5, 7.65) * mm});
            skLineSegment(sketch, "E51.10.0.11", {"start": v(428.5, -8) * mm, "end": v(432.5, -11) * mm});
            skLineSegment(sketch, "E51.10.0.12", {"start": v(357.5, -8.32) * mm, "end": v(361.72, -11) * mm});
            skLineSegment(sketch, "E51.10.0.13", {"start": v(494.05, 11) * mm, "end": v(497.5, 7.38) * mm});
            skLineSegment(sketch, "E51.10.0.14", {"start": v(424.5, -11) * mm, "end": v(428.5, -8) * mm});
            skLineSegment(sketch, "E51.10.0.15", {"start": v(497.5, -7.64) * mm, "end": v(493.8, -11) * mm});
            skLineSegment(sketch, "E51.10.0.16", {"start": v(427.6, 8) * mm, "end": v(431.6, 11) * mm});
            skLineSegment(sketch, "E51.10.0.17", {"start": v(423.6, 11) * mm, "end": v(427.6, 8) * mm});
            skLineSegment(sketch, "E51.11.0.0", {"start": v(567, -11) * mm, "end": v(504.22, -11) * mm});
            skLineSegment(sketch, "E51.11.0.1", {"start": v(500, -8.32) * mm, "end": v(500, 7.65) * mm});
            skPoint(sketch, "E51.11.0.2", {"position": v(640, 11) * mm});
            skPoint(sketch, "E51.11.0.3", {"position": v(500, -11) * mm});
            skLineSegment(sketch, "E51.11.0.4", {"start": v(640, -7.64) * mm, "end": v(640, 7.38) * mm});
            skPoint(sketch, "E51.11.0.5", {"position": v(640, -11) * mm});
            skLineSegment(sketch, "E51.11.0.6", {"start": v(636.55, 11) * mm, "end": v(574.1, 11) * mm});
            skLineSegment(sketch, "E51.11.0.7", {"start": v(636.3, -11) * mm, "end": v(575, -11) * mm});
            skLineSegment(sketch, "E51.11.0.8", {"start": v(566.1, 11) * mm, "end": v(503.7, 11) * mm});
            skPoint(sketch, "E51.11.0.9", {"position": v(500, 11) * mm});
            skLineSegment(sketch, "E51.11.0.10", {"start": v(503.7, 11) * mm, "end": v(500, 7.65) * mm});
            skLineSegment(sketch, "E51.11.0.11", {"start": v(571, -8) * mm, "end": v(575, -11) * mm});
            skLineSegment(sketch, "E51.11.0.12", {"start": v(500, -8.32) * mm, "end": v(504.22, -11) * mm});
            skLineSegment(sketch, "E51.11.0.13", {"start": v(636.55, 11) * mm, "end": v(640, 7.38) * mm});
            skLineSegment(sketch, "E51.11.0.14", {"start": v(567, -11) * mm, "end": v(571, -8) * mm});
            skLineSegment(sketch, "E51.11.0.15", {"start": v(640, -7.64) * mm, "end": v(636.3, -11) * mm});
            skLineSegment(sketch, "E51.11.0.16", {"start": v(570.1, 8) * mm, "end": v(574.1, 11) * mm});
            skLineSegment(sketch, "E51.11.0.17", {"start": v(566.1, 11) * mm, "end": v(570.1, 8) * mm});
            skLineSegment(sketch, "E51.12.0.0", {"start": v(709.5, -11) * mm, "end": v(646.72, -11) * mm});
            skLineSegment(sketch, "E51.12.0.1", {"start": v(642.5, -8.32) * mm, "end": v(642.5, 7.65) * mm});
            skPoint(sketch, "E51.12.0.2", {"position": v(782.5, 11) * mm});
            skPoint(sketch, "E51.12.0.3", {"position": v(642.5, -11) * mm});
            skLineSegment(sketch, "E51.12.0.4", {"start": v(782.5, -7.64) * mm, "end": v(782.5, 7.38) * mm});
            skPoint(sketch, "E51.12.0.5", {"position": v(782.5, -11) * mm});
            skLineSegment(sketch, "E51.12.0.6", {"start": v(779.05, 11) * mm, "end": v(716.6, 11) * mm});
            skLineSegment(sketch, "E51.12.0.7", {"start": v(778.8, -11) * mm, "end": v(717.5, -11) * mm});
            skLineSegment(sketch, "E51.12.0.8", {"start": v(708.6, 11) * mm, "end": v(646.2, 11) * mm});
            skPoint(sketch, "E51.12.0.9", {"position": v(642.5, 11) * mm});
            skLineSegment(sketch, "E51.12.0.10", {"start": v(646.2, 11) * mm, "end": v(642.5, 7.65) * mm});
            skLineSegment(sketch, "E51.12.0.11", {"start": v(713.5, -8) * mm, "end": v(717.5, -11) * mm});
            skLineSegment(sketch, "E51.12.0.12", {"start": v(642.5, -8.32) * mm, "end": v(646.72, -11) * mm});
            skLineSegment(sketch, "E51.12.0.13", {"start": v(779.05, 11) * mm, "end": v(782.5, 7.38) * mm});
            skLineSegment(sketch, "E51.12.0.14", {"start": v(709.5, -11) * mm, "end": v(713.5, -8) * mm});
            skLineSegment(sketch, "E51.12.0.15", {"start": v(782.5, -7.64) * mm, "end": v(778.8, -11) * mm});
            skLineSegment(sketch, "E51.12.0.16", {"start": v(712.6, 8) * mm, "end": v(716.6, 11) * mm});
            skLineSegment(sketch, "E51.12.0.17", {"start": v(708.6, 11) * mm, "end": v(712.6, 8) * mm});
            skLineSegment(sketch, "E51.13.0.0", {"start": v(852, -11) * mm, "end": v(789.22, -11) * mm});
            skLineSegment(sketch, "E51.13.0.1", {"start": v(785, -8.32) * mm, "end": v(785, 7.65) * mm});
            skPoint(sketch, "E51.13.0.2", {"position": v(925, 11) * mm});
            skPoint(sketch, "E51.13.0.3", {"position": v(785, -11) * mm});
            skLineSegment(sketch, "E51.13.0.4", {"start": v(925, -7.64) * mm, "end": v(925, 7.38) * mm});
            skPoint(sketch, "E51.13.0.5", {"position": v(925, -11) * mm});
            skLineSegment(sketch, "E51.13.0.6", {"start": v(921.55, 11) * mm, "end": v(859.1, 11) * mm});
            skLineSegment(sketch, "E51.13.0.7", {"start": v(921.3, -11) * mm, "end": v(860, -11) * mm});
            skLineSegment(sketch, "E51.13.0.8", {"start": v(851.1, 11) * mm, "end": v(788.7, 11) * mm});
            skPoint(sketch, "E51.13.0.9", {"position": v(785, 11) * mm});
            skLineSegment(sketch, "E51.13.0.10", {"start": v(788.7, 11) * mm, "end": v(785, 7.65) * mm});
            skLineSegment(sketch, "E51.13.0.11", {"start": v(856, -8) * mm, "end": v(860, -11) * mm});
            skLineSegment(sketch, "E51.13.0.12", {"start": v(785, -8.32) * mm, "end": v(789.22, -11) * mm});
            skLineSegment(sketch, "E51.13.0.13", {"start": v(921.55, 11) * mm, "end": v(925, 7.38) * mm});
            skLineSegment(sketch, "E51.13.0.14", {"start": v(852, -11) * mm, "end": v(856, -8) * mm});
            skLineSegment(sketch, "E51.13.0.15", {"start": v(925, -7.64) * mm, "end": v(921.3, -11) * mm});
            skLineSegment(sketch, "E51.13.0.16", {"start": v(855.1, 8) * mm, "end": v(859.1, 11) * mm});
            skLineSegment(sketch, "E51.13.0.17", {"start": v(851.1, 11) * mm, "end": v(855.1, 8) * mm});
            skLineSegment(sketch, "E51.14.0.0", {"start": v(994.5, -11) * mm, "end": v(931.72, -11) * mm});
            skLineSegment(sketch, "E51.14.0.1", {"start": v(927.5, -8.32) * mm, "end": v(927.5, 7.65) * mm});
            skPoint(sketch, "E51.14.0.2", {"position": v(1067.5, 11) * mm});
            skPoint(sketch, "E51.14.0.3", {"position": v(927.5, -11) * mm});
            skLineSegment(sketch, "E51.14.0.4", {"start": v(1067.5, -7.64) * mm, "end": v(1067.5, 7.38) * mm});
            skPoint(sketch, "E51.14.0.5", {"position": v(1067.5, -11) * mm});
            skLineSegment(sketch, "E51.14.0.6", {"start": v(1064.05, 11) * mm, "end": v(1001.6, 11) * mm});
            skLineSegment(sketch, "E51.14.0.7", {"start": v(1063.8, -11) * mm, "end": v(1002.5, -11) * mm});
            skLineSegment(sketch, "E51.14.0.8", {"start": v(993.6, 11) * mm, "end": v(931.2, 11) * mm});
            skPoint(sketch, "E51.14.0.9", {"position": v(927.5, 11) * mm});
            skLineSegment(sketch, "E51.14.0.10", {"start": v(931.2, 11) * mm, "end": v(927.5, 7.65) * mm});
            skLineSegment(sketch, "E51.14.0.11", {"start": v(998.5, -8) * mm, "end": v(1002.5, -11) * mm});
            skLineSegment(sketch, "E51.14.0.12", {"start": v(927.5, -8.32) * mm, "end": v(931.72, -11) * mm});
            skLineSegment(sketch, "E51.14.0.13", {"start": v(1064.05, 11) * mm, "end": v(1067.5, 7.38) * mm});
            skLineSegment(sketch, "E51.14.0.14", {"start": v(994.5, -11) * mm, "end": v(998.5, -8) * mm});
            skLineSegment(sketch, "E51.14.0.15", {"start": v(1067.5, -7.64) * mm, "end": v(1063.8, -11) * mm});
            skLineSegment(sketch, "E51.14.0.16", {"start": v(997.6, 8) * mm, "end": v(1001.6, 11) * mm});
            skLineSegment(sketch, "E51.14.0.17", {"start": v(993.6, 11) * mm, "end": v(997.6, 8) * mm});
            skLineSegment(sketch, "E51.direction1", {"start": v(-1067.5, -11) * mm, "end": v(-925, -11) * mm, "construction": true});
            skSolve(sketch);
        }
        {
            var Q0;
            Q0 = qSketchRegion(id + "F5", true);
            extrude(context, id + "F6", {"entities" : qUnion([Q0]), "operationType" : NewBodyOperationType.ADD, "depth" : 825 * mm, "hasSecondDirection" : true, "secondDirectionOppositeDirection" : true, "secondDirectionDepth" : 487.5 * mm});
        }
    });
